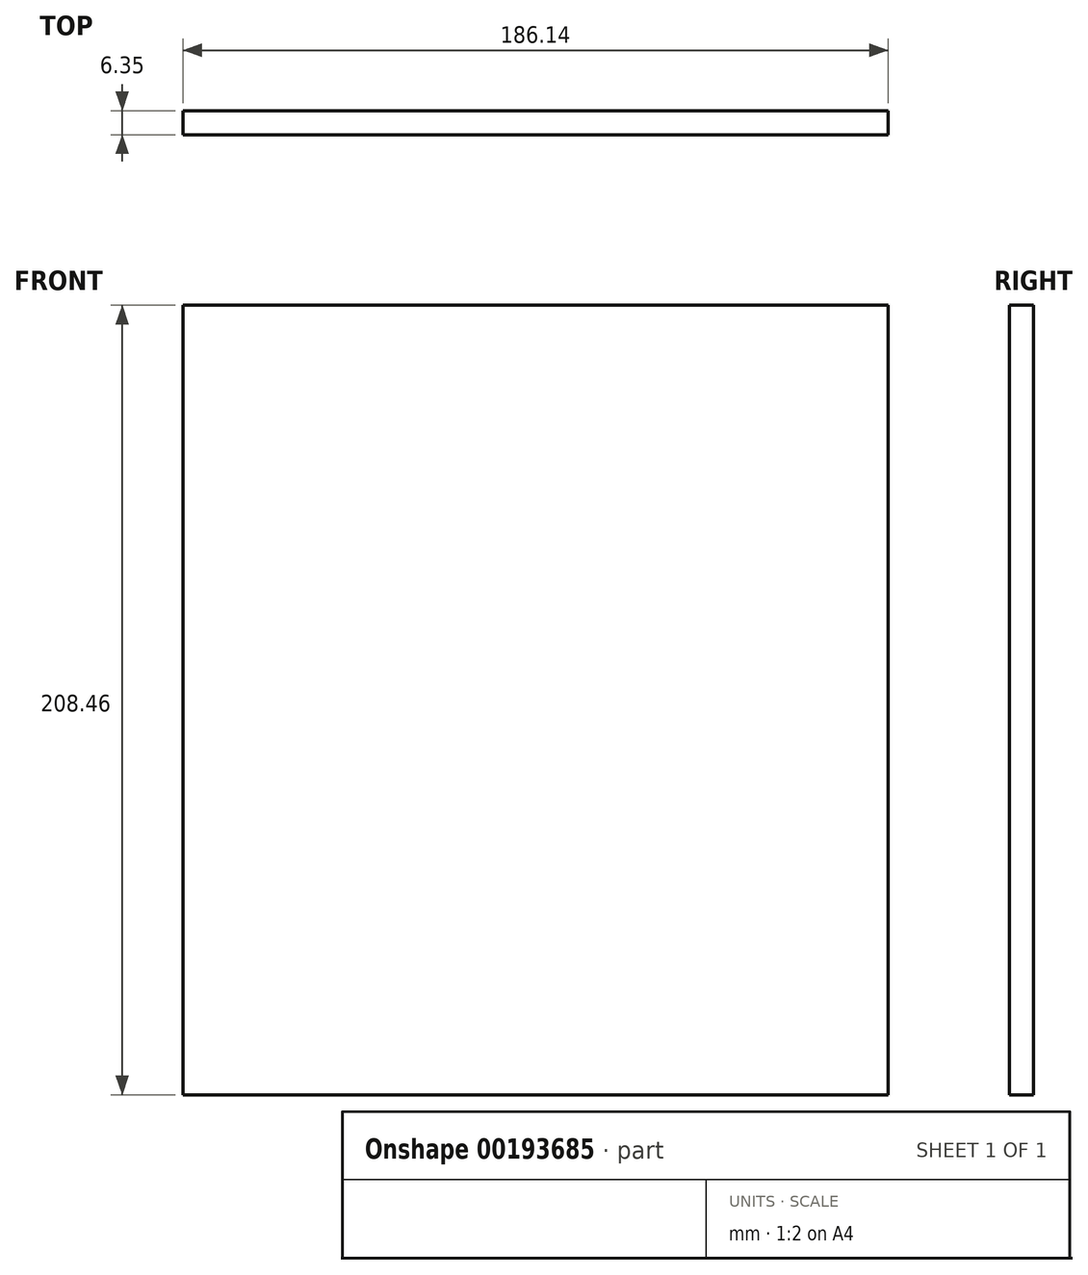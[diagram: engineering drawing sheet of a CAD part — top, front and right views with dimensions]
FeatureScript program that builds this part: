
annotation { "Feature Type Name" : "Feature", "Feature Type Description" : "" }
export const myFeature = defineFeature(function(context is Context, id is Id, definition is map)
    precondition{}
    {
        {
            var Q0;
            Q0=qCreatedBy(makeId("Front.planeOp"),FACE);
            var sketch = newSketch(context, id + "F0", { "sketchPlane" : qUnion([Q0])});
            skLineSegment(sketch, "E0.bottom", {"start": v(93.07, 104.23) * mm, "end": v(-93.07, 104.23) * mm});
            skLineSegment(sketch, "E0.top", {"start": v(93.07, -104.23) * mm, "end": v(-93.07, -104.23) * mm});
            skLineSegment(sketch, "E0.left", {"start": v(93.07, 104.23) * mm, "end": v(93.07, -104.23) * mm});
            skLineSegment(sketch, "E0.right", {"start": v(-93.07, 104.23) * mm, "end": v(-93.07, -104.23) * mm});
            skPoint(sketch, "E0.middle", {"position": v(0, 0) * mm});
            skSolve(sketch);
        }
        {
            var Q0;
            Q0=makeQuery(id+"F0.imprint","IMPRINT",FACE,{"disambiguationData":[TD([[makeQuery(id+"F0.imprint","IMPRINT",EDGE,{"derivedFrom":sQuery(id+"F0.wireOp",EDGE,"E0.bottom")}),1.0]])]});
            extrude(context, id + "F1", {"entities" : qUnion([Q0]), "depth" : 6.35 * mm});
        }
    });
